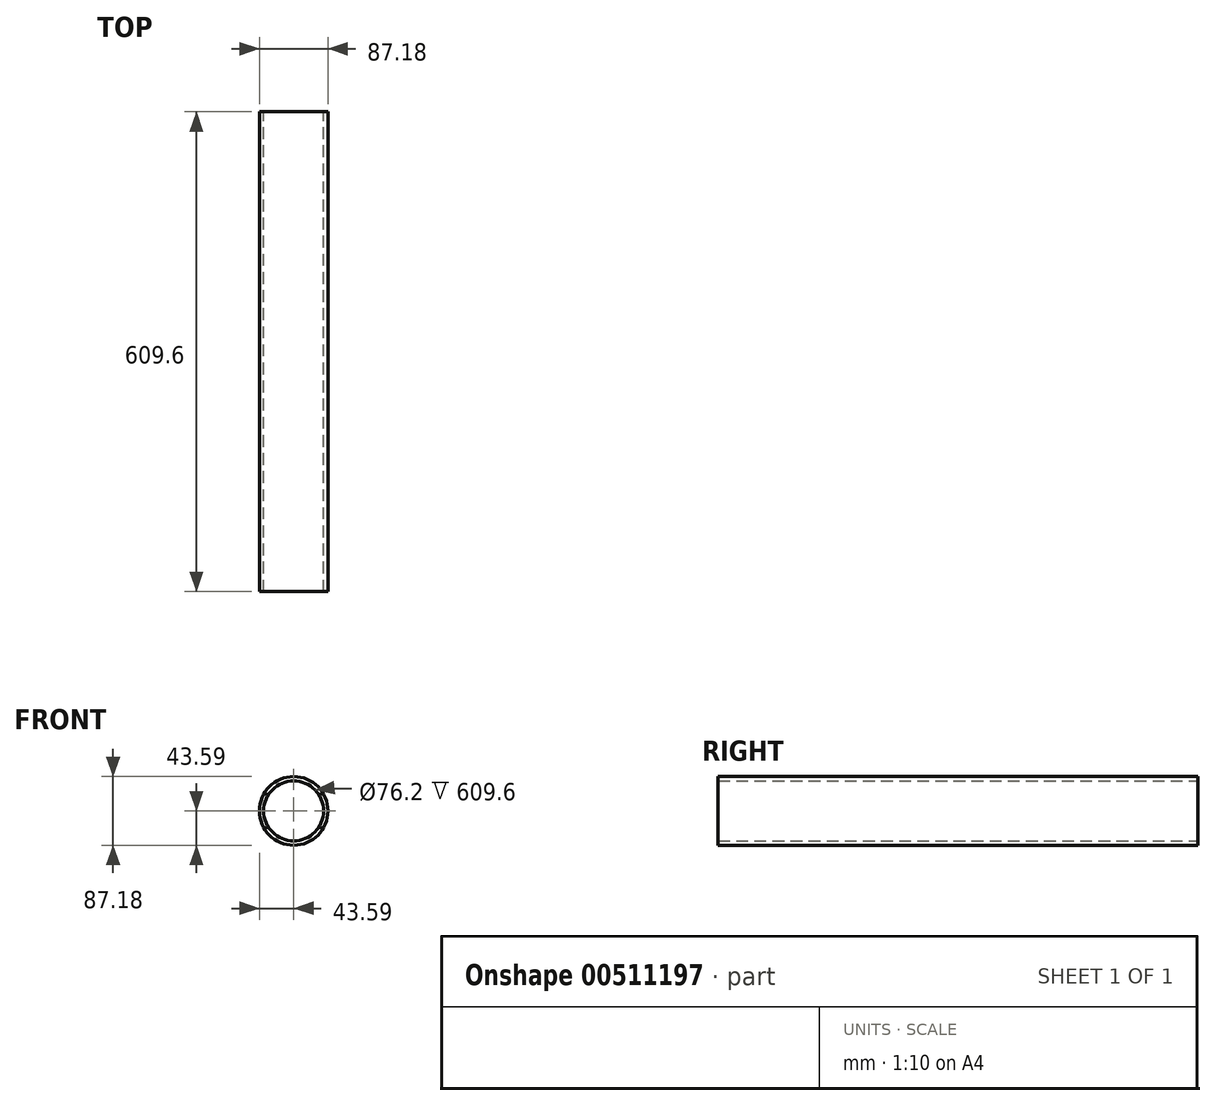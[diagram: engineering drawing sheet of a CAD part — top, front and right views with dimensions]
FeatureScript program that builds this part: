
annotation { "Feature Type Name" : "Feature", "Feature Type Description" : "" }
export const myFeature = defineFeature(function(context is Context, id is Id, definition is map)
    precondition{}
    {
        {
            var Q0;
            Q0=qCreatedBy(makeId("Front.planeOp"),FACE);
            var sketch = newSketch(context, id + "F0", { "sketchPlane" : qUnion([Q0])});
            skCircle(sketch, "E0", {"center": v(0, 0) * mm, "radius": 38.1 * mm});
            skCircle(sketch, "E1", {"center": v(0, 0) * mm, "radius": 43.59 * mm});
            skSolve(sketch);
        }
        {
            var Q0;
            Q0=qSketchRegion(id+"F0",true);
            extrude(context, id + "F1", {"entities" : qUnion([Q0]), "endBound" : BoundingType.SYMMETRIC, "depth" : 609.6 * mm});
        }
    });
